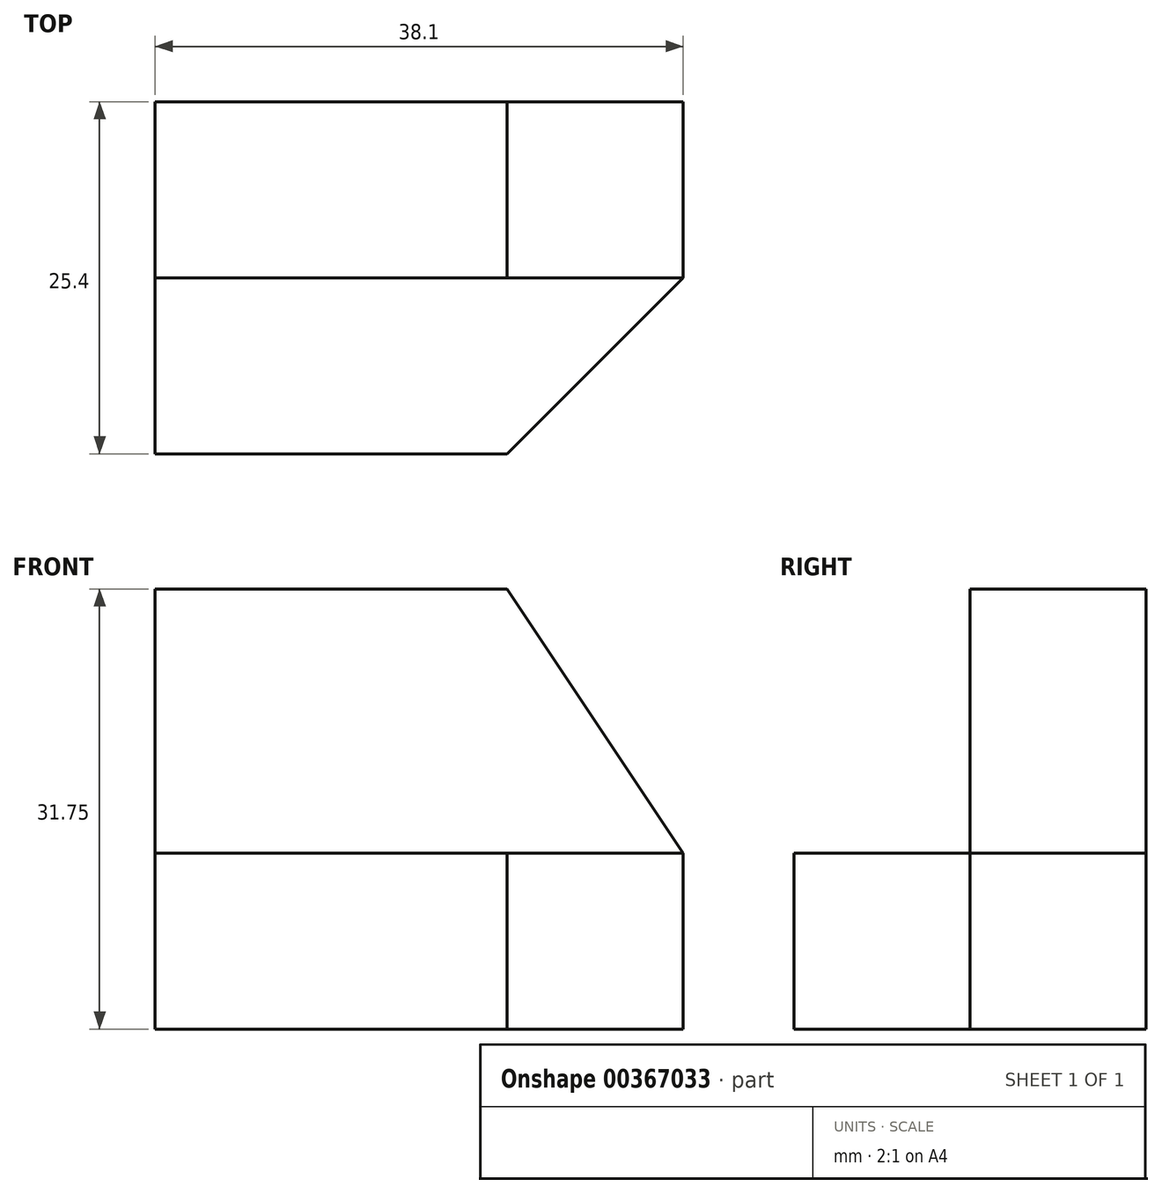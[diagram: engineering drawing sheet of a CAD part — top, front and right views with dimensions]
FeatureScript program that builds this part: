
annotation { "Feature Type Name" : "Feature", "Feature Type Description" : "" }
export const myFeature = defineFeature(function(context is Context, id is Id, definition is map)
    precondition{}
    {
        {
            var Q0;
            Q0=qCreatedBy(makeId("Right.planeOp"),FACE);
            var sketch = newSketch(context, id + "F0", { "sketchPlane" : qUnion([Q0])});
            skLineSegment(sketch, "E0", {"start": v(0, 0) * mm, "end": v(25.4, 0) * mm});
            skLineSegment(sketch, "E1", {"start": v(25.4, 0) * mm, "end": v(25.4, 31.75) * mm});
            skLineSegment(sketch, "E2", {"start": v(25.4, 31.75) * mm, "end": v(12.7, 31.75) * mm});
            skLineSegment(sketch, "E3", {"start": v(12.7, 31.75) * mm, "end": v(12.7, 12.7) * mm});
            skLineSegment(sketch, "E4", {"start": v(12.7, 12.7) * mm, "end": v(0, 12.7) * mm});
            skLineSegment(sketch, "E5", {"start": v(0, 12.7) * mm, "end": v(0, 0) * mm});
            skSolve(sketch);
        }
        {
            var Q0;
            Q0 = qSketchRegion(id + "F0", true);
            extrude(context, id + "F1", {"entities" : qUnion([Q0]), "depth" : 38.1 * mm});
        }
        {
            var Q0;
            Q0=makeQuery(id+"F1.opExtrude","SWEPT_FACE",FACE,{"disambiguationData":[OSD([sQuery(id+"F0.wireOp",EDGE,"E4")])]});
            var sketch = newSketch(context, id + "F2", { "sketchPlane" : qUnion([Q0])});
            skLineSegment(sketch, "E6", {"start": v(38.1, 12.7) * mm, "end": v(25.4, 0) * mm});
            skSolve(sketch);
        }
        {
            var Q0;
            Q0=makeQuery(id+"F1.opExtrude","SWEPT_FACE",FACE,{"disambiguationData":[OSD([sQuery(id+"F0.wireOp",EDGE,"E3")])]});
            var sketch = newSketch(context, id + "F3", { "sketchPlane" : qUnion([Q0])});
            skLineSegment(sketch, "E7", {"start": v(38.1, 12.7) * mm, "end": v(25.4, 31.75) * mm});
            skSolve(sketch);
        }
        {
            var Q0;
            {var subQ0=sQuery(id+"F3.wireOp",EDGE,"E7");Q0=makeQuery(id+"F3.imprint","IMPRINT",FACE,{"disambiguationData":[TD([[makeQuery(id+"F3.imprint","IMPRINT",EDGE,{"derivedFrom":subQ0}),-1.0]])]});}
            extrude(context, id + "F4", {"entities" : qUnion([Q0]), "operationType" : NewBodyOperationType.REMOVE, "oppositeDirection" : true, "depth" : 25.4 * mm});
        }
        {
            var Q0;
            {var subQ0=sQuery(id+"F2.wireOp",EDGE,"E6");Q0=makeQuery(id+"F2.imprint","IMPRINT",FACE,{"disambiguationData":[TD([[makeQuery(id+"F2.imprint","IMPRINT",EDGE,{"derivedFrom":subQ0}),1.0]])]});}
            extrude(context, id + "F5", {"entities" : qUnion([Q0]), "operationType" : NewBodyOperationType.REMOVE, "oppositeDirection" : true, "depth" : 25.4 * mm});
        }
    });
